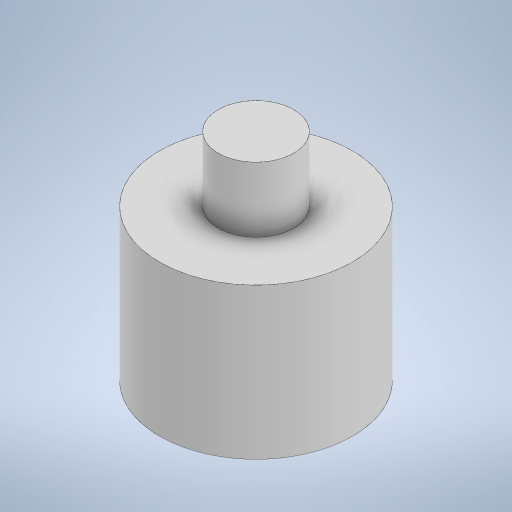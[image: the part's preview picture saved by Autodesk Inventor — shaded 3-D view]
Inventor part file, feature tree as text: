
AUTODESK INVENTOR PART (.ipt)
format: ipt  version: 2023 (Build 270158000, 158)  size: 220,160 bytes
history: native  units: in
note: dims shown in document units (in); Inventor stores cm internally (conversion verified against a paired STEP export)
features: extrude x2, sketch x2, projected_geometry x1
ambient origin geometry x8: Origin, YZ Plane, XZ Plane, XY Plane, X Axis, Y Axis, Z Axis, Center Point
bodies: Solid1 (feature_tree)
feature tree (5):
  extrude  "Extrusion1"  Depth=0.6102in TaperAngle=0.0deg
  extrude  "Extrusion2"  Depth=1.4173in TaperAngle=0.0deg
  sketch  "Sketch1"  dims[d0=0.7087in d1=0.6102in d2=0.0in]
  sketch  "Sketch2"  dims[d3=1.811in d4=1.4173in d5=0.0in]
  projected_geometry  "Projected Loop1"
